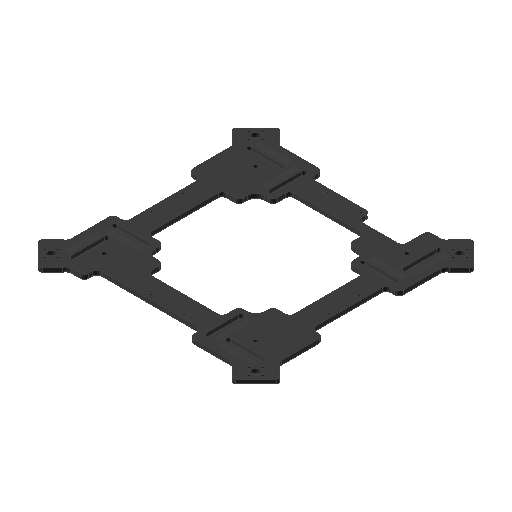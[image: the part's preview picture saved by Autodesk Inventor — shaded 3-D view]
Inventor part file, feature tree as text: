
AUTODESK INVENTOR PART (.ipt)
format: ipt  version: 2023 (Build 270158000, 158)  size: 1,357,312 bytes
history: native  units: mm
features: sketch x4, extrude x3, fillet x3, chamfer x1, mirror x1
ambient origin geometry x8: Origin, YZ Plane, XZ Plane, XY Plane, X Axis, Y Axis, Z Axis, Center Point
bodies: Solid1 (feature_tree)
feature tree (12):
  extrude  "Extrusion1"  Depth=3.0mm
  extrude  "Extrusion2"  Depth=10.0mm TaperAngle=0.0deg
  sketch  "Sketch4"  dims[d7=3.0mm]
  chamfer  "Chamfer1"  Distance=20.0mm
  fillet  "Fillet1"  Radius=10.0mm
  fillet  "Fillet2"  Radius=6.0mm
  extrude  "Extrusion3"  Depth=3.0mm
  fillet  "Fillet3"  Radius=7.0mm
  sketch  "Sketch2"  dims[d2=20.0mm d3=3.0mm]
  sketch  "Sketch3"  dims[d4=20.0mm d5=10.0mm d6=0.0mm]
  sketch  "Sketch5"  dims[d8=18.5mm d9=20.0mm d10=10.0mm d11=0.0mm d12=6.0mm d13=2.0mm d14=45.0deg d15=3.0mm d16=7.0mm d17=125.0mm d18=15.0mm d19=15.0mm d20=90.0mm d21=15.0mm d22=15.0mm d23=125.0mm d24=12.0mm d25=12.0mm d26=10.0mm d27=0.0mm d28=5.0mm]
  mirror  "Mirror7"
